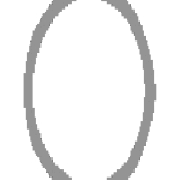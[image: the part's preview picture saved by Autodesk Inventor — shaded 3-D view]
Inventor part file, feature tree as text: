
AUTODESK INVENTOR PART (.ipt)
format: ipt  version: 2021 (Build 250183000, 183)  size: 109,568 bytes
history: native  units: in
note: dims shown in document units (in); Inventor stores cm internally (conversion verified against a paired STEP export)
features: other x4, sketch x3, plane x1
ambient origin geometry x8: Origin, YZ Plane, XZ Plane, XY Plane, X Axis, Y Axis, Z Axis, Center Point
bodies: Solid1 (feature_tree), Body (feature_tree)
feature tree (8):
  other  "Driven Length"
  other  "Frame Generator"
  other  "Start Plane"
  other  "End Plane"
  sketch  "Sketch"  dims[d2=25.5539in d4=-0.0in d5=25.5539in d6=0.12in d7=0.0in d8=90.0deg d9=25.5539in]
  sketch  "Sketch2"  dims[d0=1.0in]
  plane  "Work Plane3"
  sketch  "Sketch3"  dims[d1=0.065in]
